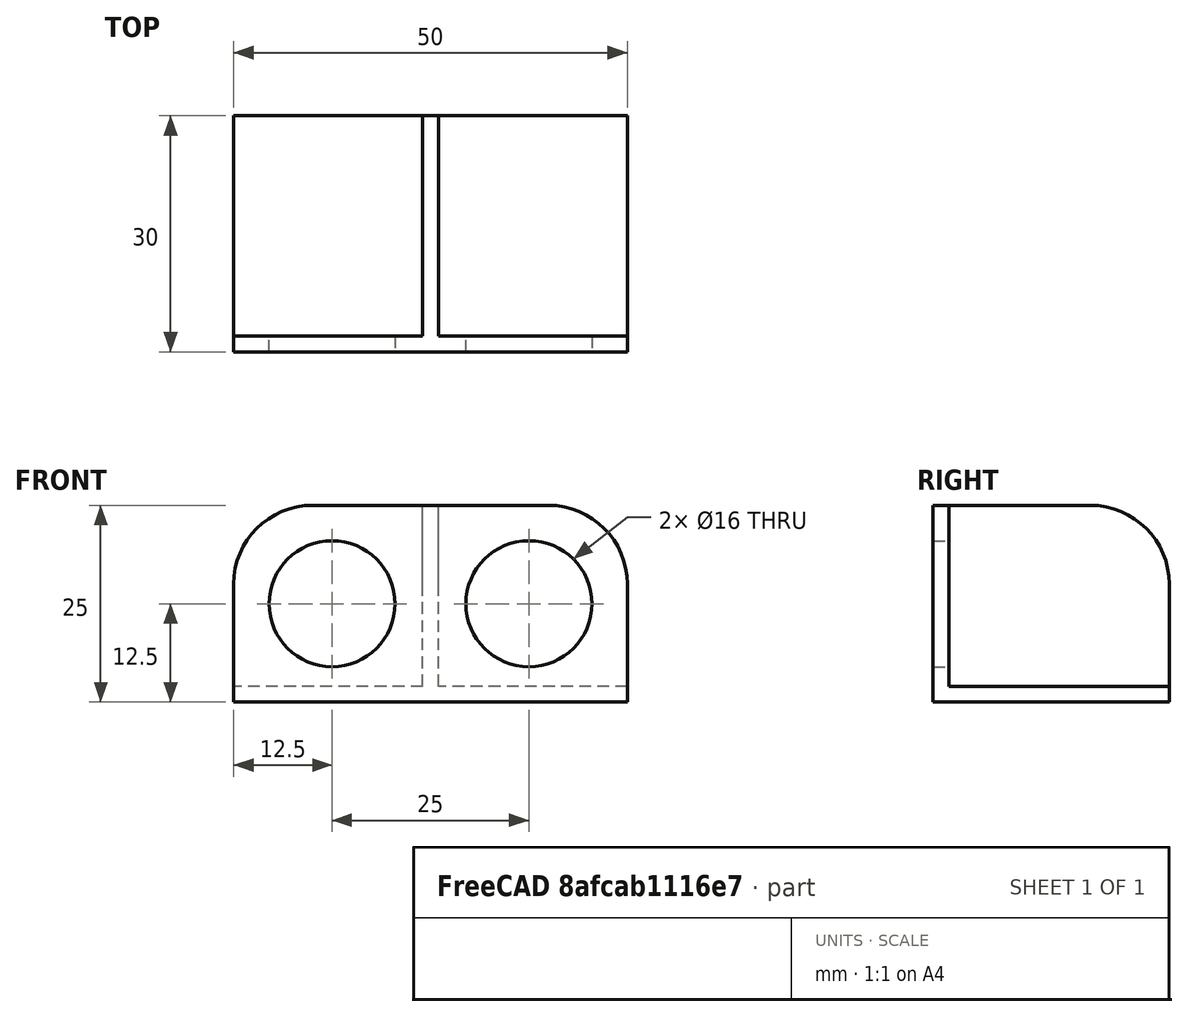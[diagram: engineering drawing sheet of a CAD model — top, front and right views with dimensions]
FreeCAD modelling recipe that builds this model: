
FCSTD DOCUMENT  (FreeCAD 0.21R33771 (Git))
Label: TasterHalterung
License: All rights reserved
LicenseURL: http://en.wikipedia.org/wiki/All_rights_reserved
objects: Part::Box×3, Part::Cylinder×2, Part::MultiFuse×2, Part::Fillet×2, Part::Cut×1, Part::Refine×1
note: 11 computed .brp shape members not serialized (recipe doc carries the construction recipe); baked Part::Feature solids carry a one-line shape summary decoded from their .brp

FEATURE [Part::Box] Box  label="Cube"
  AttacherType = Attacher::AttachEngine3D
  Height = 2
  Length = 50
  Width = 30
FEATURE [Part::Box] Box001  label="Cube001"
  AttacherType = Attacher::AttachEngine3D
  Height = 25
  Length = 50
  Width = 2
FEATURE [Part::Cylinder] Cylinder
  Angle = 360
  AttacherType = Attacher::AttachEngine3D
  FirstAngle = 0
  Height = 10
  Placement = pos=(12.5,4,12.5) rot=(1,0,0;1.5708rad)
  Radius = 8
  SecondAngle = 0
FEATURE [Part::Cylinder] Cylinder001
  Angle = 360
  AttacherType = Attacher::AttachEngine3D
  FirstAngle = 0
  Height = 10
  Placement = pos=(37.5,4,12.5) rot=(1,0,0;1.5708rad)
  Radius = 8
  SecondAngle = 0
FEATURE [Part::MultiFuse] Fusion
  Shapes = -> [Cylinder001,Cylinder]
FEATURE [Part::Box] Box002  label="Cube002"
  AttacherType = Attacher::AttachEngine3D
  Height = 25
  Length = 2
  Placement = pos=(24,0,0) rot=(0,0,1;0rad)
  Width = 30
FEATURE [Part::Fillet] Fillet
  Base = -> Box002
  Edges = 1 edges r=10: [Edge12]
FEATURE [Part::Fillet] Fillet001
  Base = -> Box001
  Edges = 2 edges r=10: [Edge2,Edge6]
FEATURE [Part::MultiFuse] Fusion001
  Shapes = -> [Box,Fillet,Fillet001]
FEATURE [Part::Cut] Cut
  Base = -> Fusion001
  Tool = -> Fusion
FEATURE [Part::Refine] Cut001
  Source = -> Cut
